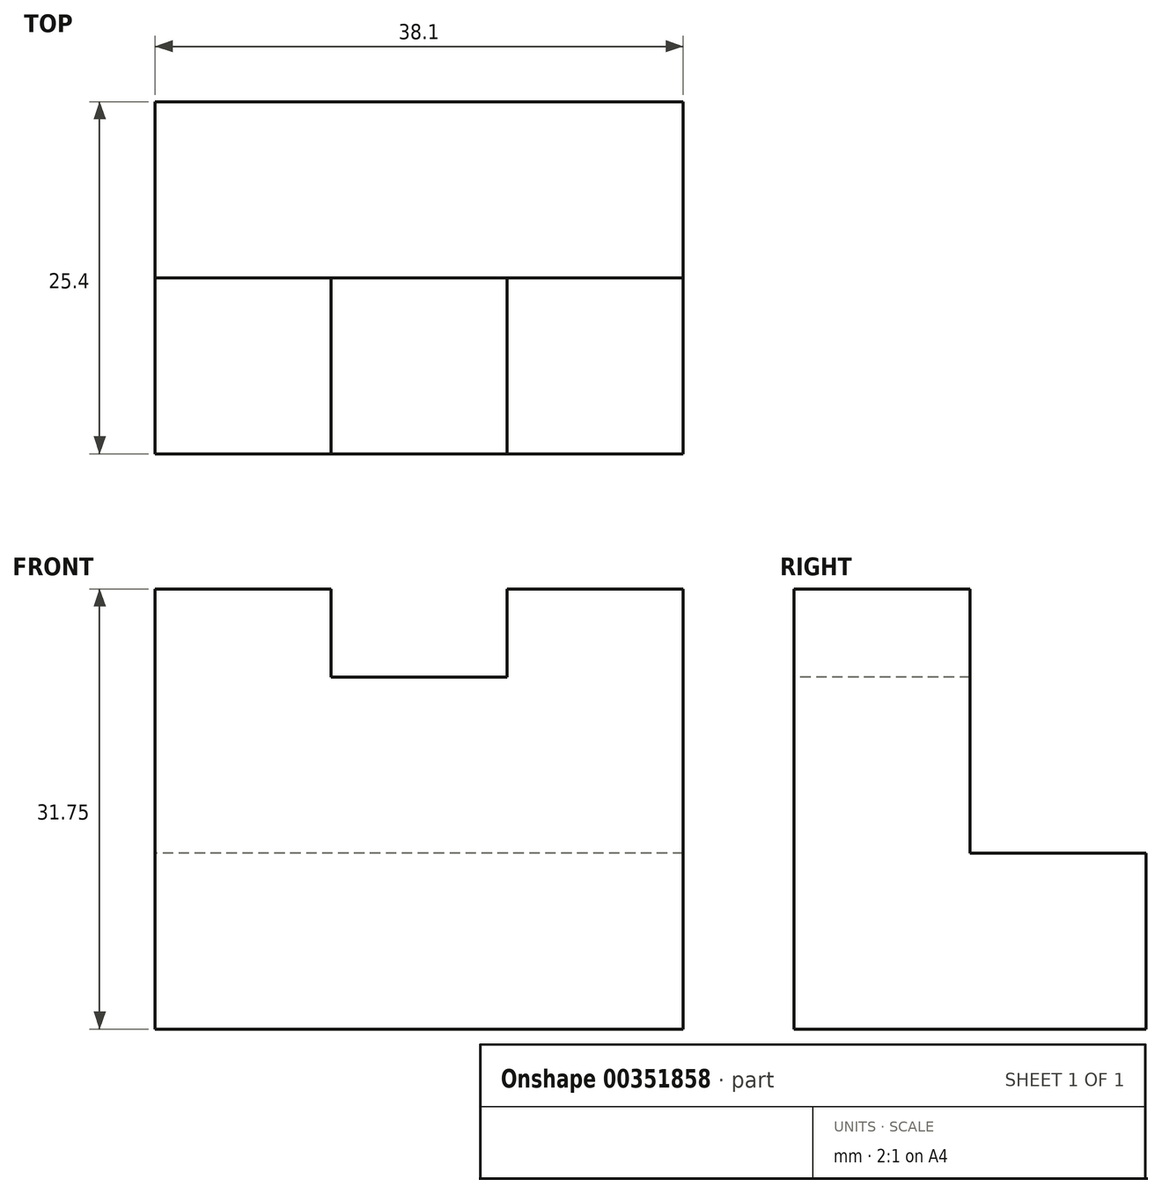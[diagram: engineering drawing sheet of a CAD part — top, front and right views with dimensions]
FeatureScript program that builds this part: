
annotation { "Feature Type Name" : "Feature", "Feature Type Description" : "" }
export const myFeature = defineFeature(function(context is Context, id is Id, definition is map)
    precondition{}
    {
        {
            var Q0;
            Q0=qCreatedBy(makeId("Right.planeOp"),FACE);
            var sketch = newSketch(context, id + "F0", { "sketchPlane" : qUnion([Q0])});
            skLineSegment(sketch, "E0", {"start": v(0, 0) * mm, "end": v(25.4, 0) * mm});
            skLineSegment(sketch, "E1", {"start": v(25.4, 0) * mm, "end": v(25.4, 12.7) * mm});
            skLineSegment(sketch, "E2", {"start": v(25.4, 12.7) * mm, "end": v(12.7, 12.7) * mm});
            skLineSegment(sketch, "E3", {"start": v(12.7, 12.7) * mm, "end": v(12.7, 31.75) * mm});
            skLineSegment(sketch, "E4", {"start": v(12.7, 31.75) * mm, "end": v(0, 31.75) * mm});
            skLineSegment(sketch, "E5", {"start": v(0, 31.75) * mm, "end": v(0, 0) * mm});
            skSolve(sketch);
        }
        {
            var Q0;
            Q0 = qSketchRegion(id + "F0", true);
            extrude(context, id + "F1", {"entities" : qUnion([Q0]), "depth" : 38.1 * mm});
        }
        {
            var Q0;
            Q0=makeQuery(id+"F1.opExtrude","SWEPT_FACE",FACE,{"disambiguationData":[OSD([sQuery(id+"F0.wireOp",EDGE,"E5")])]});
            var sketch = newSketch(context, id + "F2", { "sketchPlane" : qUnion([Q0])});
            skLineSegment(sketch, "E6.bottom", {"start": v(12.7, 31.75) * mm, "end": v(25.4, 31.75) * mm});
            skLineSegment(sketch, "E6.top", {"start": v(12.7, 25.4) * mm, "end": v(25.4, 25.4) * mm});
            skLineSegment(sketch, "E6.left", {"start": v(12.7, 31.75) * mm, "end": v(12.7, 25.4) * mm});
            skLineSegment(sketch, "E6.right", {"start": v(25.4, 31.75) * mm, "end": v(25.4, 25.4) * mm});
            skSolve(sketch);
        }
        {
            var Q0;
            Q0=makeQuery(id+"F2.imprint","IMPRINT",FACE,{"disambiguationData":[TD([[makeQuery(id+"F2.imprint","IMPRINT",EDGE,{"derivedFrom":sQuery(id+"F2.wireOp",EDGE,"E6.bottom")}),1.0]])]});
            extrude(context, id + "F3", {"entities" : qUnion([Q0]), "operationType" : NewBodyOperationType.REMOVE, "oppositeDirection" : true, "depth" : 25.4 * mm});
        }
    });
